# Revit family: Kosz_nascienny_23 l stal szlachetna matowa
name_source: partatom
category: Furniture
units: mm (PartAtom-declared; Revit-internal decimal feet)

## family parameters
Always vertical = Yes
Cut with Voids When Loaded = No
Host = Wall
Room Calculation Point = No
Shared = No

## types (1)
- WB23SHB
    Depth / Glebokosc = 155 mm  [stored 0.50853 ft]
    Description = Kosz naścienny 23 l stal szlachetna matowa
    Height / Wysokosc = 435 mm  [stored 1.42717 ft]
    Manufacturer = FANECO.com
    Manufacturer code / Kod producenta = 5901764291244
    Material = Stal nierdzewna szczotkowana
    Material finish / Wykonczenie = Stal nierdzewna 430 szczotkowana, mat.
    Product code / Kod produktu = WB23SHB
    Type Comments = Kosz naścienny 23 l stal szlachetna matowa
    URL = https://faneco.com
    Weight / Waga = 3.25 kg
    Width / Szerokosc = 350 mm  [stored 1.14829 ft]

note: [stored X ft] marks values corroborated as IEEE doubles in the binary element streams (Revit-internal decimal feet)

## geometry (parser evidence)
native form markers: Sweep x11
no freeform markers — native parametric forms only
